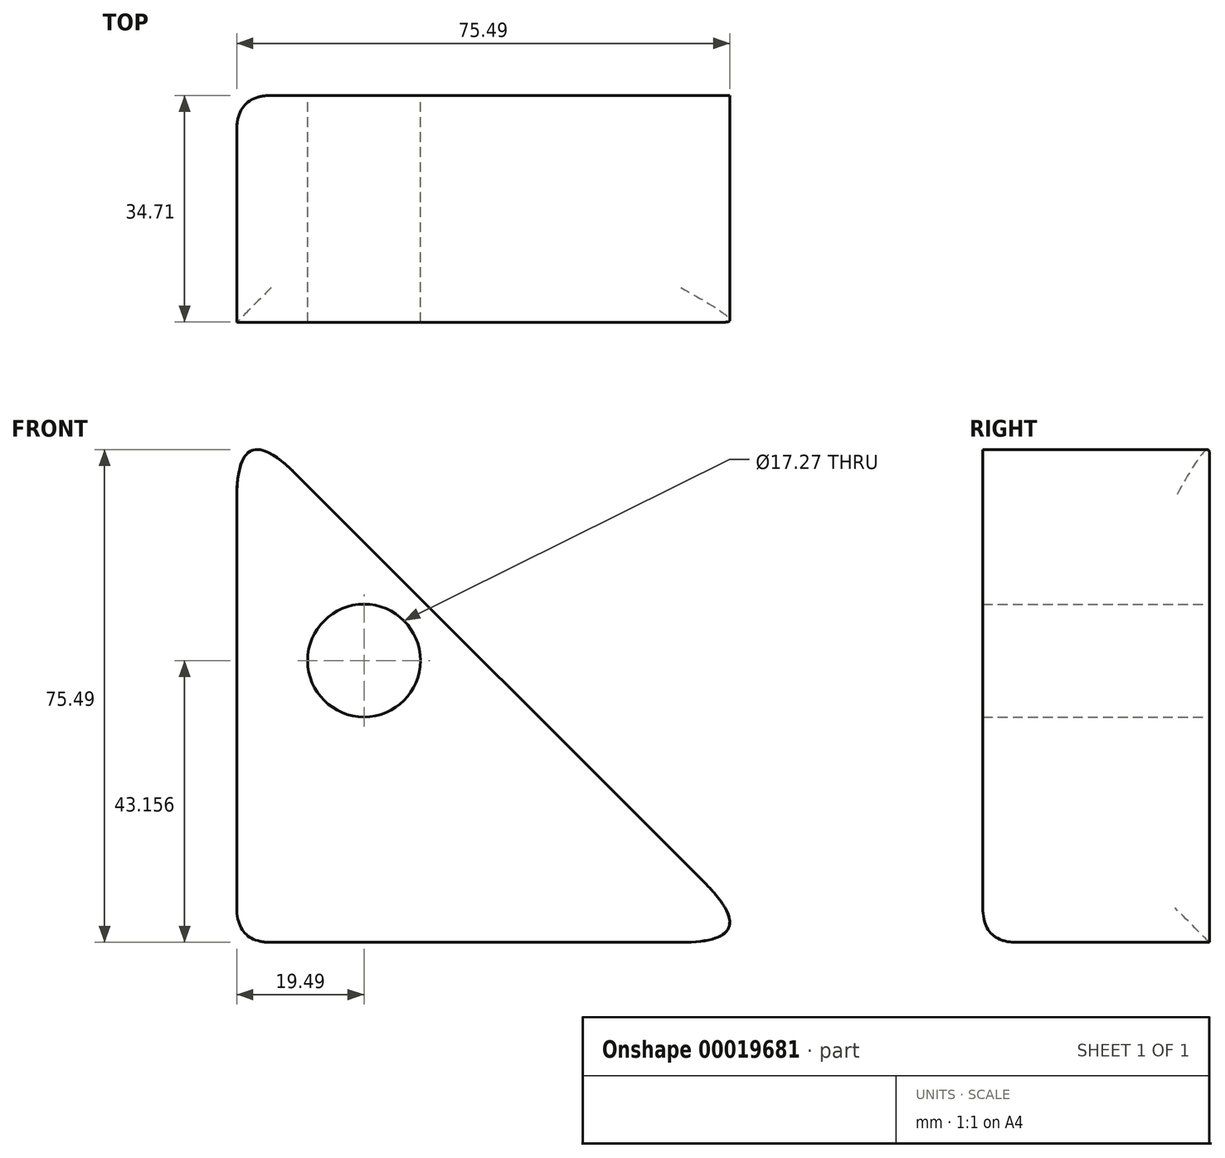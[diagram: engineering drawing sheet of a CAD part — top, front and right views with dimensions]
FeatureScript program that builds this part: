
annotation { "Feature Type Name" : "Feature", "Feature Type Description" : "" }
export const myFeature = defineFeature(function(context is Context, id is Id, definition is map)
    precondition{}
    {
        {
            var Q0;
            Q0=qCreatedBy(makeId("Front.planeOp"),FACE);
            var sketch = newSketch(context, id + "F0", { "sketchPlane" : qUnion([Q0])});
            skPoint(sketch, "E0.start.orphan", {"position": v(-172.04, 0) * mm});
            skLineSegment(sketch, "E1", {"start": v(-99.14, 0) * mm, "end": v(-99.14, -80.78) * mm});
            skLineSegment(sketch, "E2", {"start": v(-99.14, -80.78) * mm, "end": v(-179.93, -80.78) * mm});
            skLineSegment(sketch, "E3", {"start": v(-179.93, -80.78) * mm, "end": v(-179.93, 0) * mm});
            skLineSegment(sketch, "E4", {"start": v(-179.93, 0) * mm, "end": v(-99.14, 0) * mm});
            skLineSegment(sketch, "E5", {"start": v(-179.93, 0) * mm, "end": v(-99.14, -80.78) * mm});
            skSolve(sketch);
        }
        {
            var Q0;
            Q0=makeQuery(id+"F0.imprint","IMPRINT",FACE,{"disambiguationData":[TD([[makeQuery(id+"F0.imprint","IMPRINT",EDGE,{"derivedFrom":sQuery(id+"F0.wireOp",EDGE,"E2")}),-1.0]])]});
            var Q1;
            Q1 = qSketchRegion(id + "FXSASuO6Ppy86L3_1", true);
            extrude(context, id + "F1", {"entities" : qUnion([Q0, Q1]), "depth" : 34.7 * mm});
        }
        {
            var Q0;
            Q0=makeQuery(id+"F1.opExtrude","SWEPT_EDGE",EDGE,{"disambiguationData":[OSD([sQuery(id+"F0.wireOp",EDGE,"E1"),sQuery(id+"F0.wireOp",EDGE,"E2"),sQuery(id+"F0.wireOp",EDGE,"E5")])]});
            var Q1;
            Q1=makeQuery(id+"F1.opExtrude","SWEPT_EDGE",EDGE,{"disambiguationData":[OSD([sQuery(id+"F0.wireOp",EDGE,"E2"),sQuery(id+"F0.wireOp",EDGE,"E3")])]});
            var Q2;
            Q2=makeQuery(id+"F1.opExtrude","CAP_EDGE",EDGE,{"disambiguationData":[OSD([sQuery(id+"F0.wireOp",EDGE,"E2")])],"isStart":false});
            var Q3;
            Q3=makeQuery(id+"F1.opExtrude","CAP_EDGE",EDGE,{"disambiguationData":[OSD([sQuery(id+"F0.wireOp",EDGE,"E3")])],"isStart":true});
            var Q4;
            Q4=makeQuery(id+"F1.opExtrude","SWEPT_EDGE",EDGE,{"disambiguationData":[OSD([sQuery(id+"F0.wireOp",EDGE,"E3"),sQuery(id+"F0.wireOp",EDGE,"E4"),sQuery(id+"F0.wireOp",EDGE,"E5")])]});
            fillet(context, id + "F2", {"entities" : qUnion([Q0, Q1, Q2, Q3, Q4]), "radius" : 5.3 * mm, "tangentPropagation" : true, "rho" : 0.5, "crossSection" : FilletCrossSection.CONIC, "allowEdgeOverflow" : false});
        }
        {
            var Q0;
            Q0=makeQuery(id+"F1.opExtrude","CAP_FACE",FACE,{"disambiguationData":[OSD([sQuery(id+"F0.wireOp",EDGE,"E2"),sQuery(id+"F0.wireOp",EDGE,"E3"),sQuery(id+"F0.wireOp",EDGE,"E5")])],"isStart":true});
            var sketch = newSketch(context, id + "F3", { "sketchPlane" : qUnion([Q0])});
            skCircle(sketch, "E6", {"center": v(160.44, -37.62) * mm, "radius": 8.13 * mm});
            skSolve(sketch);
        }
        {
            var Q0;
            Q0=sQuery(id+"F3.wireOp",VERTEX,"E6.center");
            var Q1;
            Q1=makeQuery(id+"F1.opExtrude","SWEPT_BODY",BODY,{"disambiguationData":[OSD([sQuery(id+"F0.wireOp",EDGE,"E2"),sQuery(id+"F0.wireOp",EDGE,"E3"),sQuery(id+"F0.wireOp",EDGE,"E5")])]});
            hole(context, id + "F4", {"style" : HoleStyle.SIMPLE, "holeDiameter" : 17.27 * mm, "endStyle" : HoleEndStyle.THROUGH, "locations" : qUnion([Q0]), "scope" : qUnion([Q1])});
        }
    });
